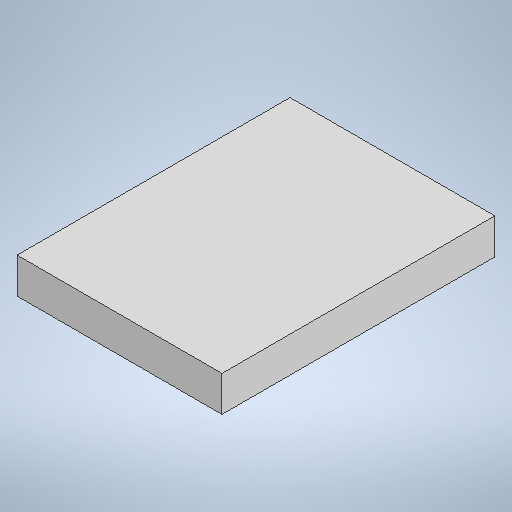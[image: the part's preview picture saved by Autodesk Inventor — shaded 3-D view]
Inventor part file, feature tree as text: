
AUTODESK INVENTOR PART (.ipt)
format: ipt  version: 2025.1 (Build 291241000, 241)  size: 222,208 bytes
history: native  units: mm
features: extrude x1, sketch x1
ambient origin geometry x8: Origin, YZ Plane, XZ Plane, XY Plane, X Axis, Y Axis, Z Axis, Center Point
bodies: Volumenkörper1 (feature_tree)
feature tree (2):
  extrude  "Extrusion1"  Depth=180.5mm
  sketch  "Skizze1"  dims[d0=135.5mm d1=180.5mm d2=23.5mm d3=0.0mm]
